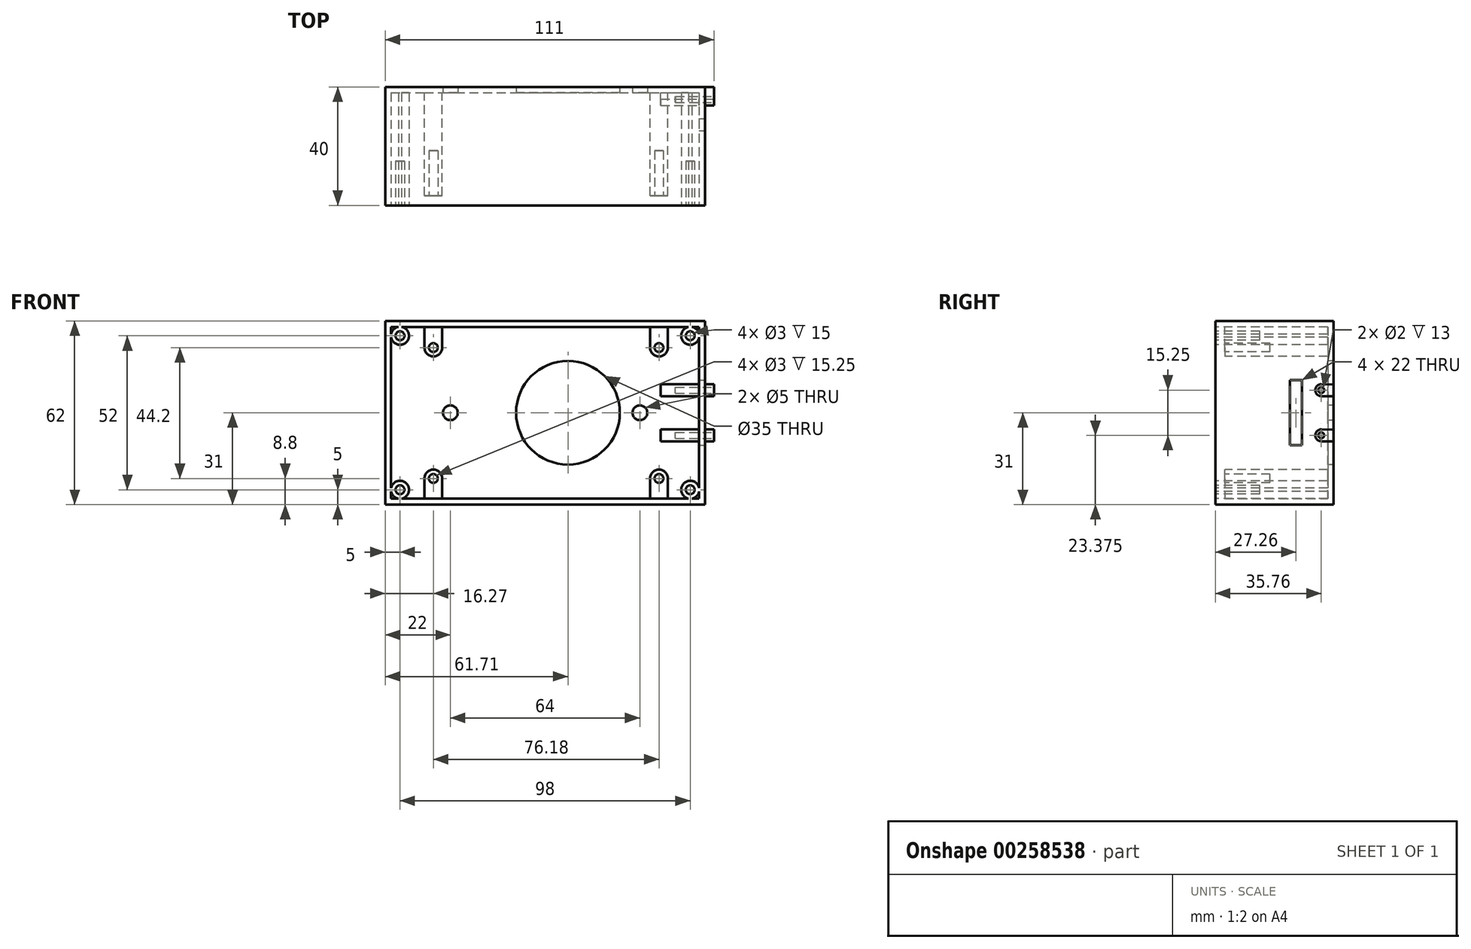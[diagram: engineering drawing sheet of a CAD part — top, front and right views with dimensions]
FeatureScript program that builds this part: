
annotation { "Feature Type Name" : "Feature", "Feature Type Description" : "" }
export const myFeature = defineFeature(function(context is Context, id is Id, definition is map)
    precondition{}
    {
        {
            var Q0;
            Q0=qCreatedBy(makeId("Front.planeOp"),FACE);
            var sketch = newSketch(context, id + "F0", { "sketchPlane" : qUnion([Q0])});
            skLineSegment(sketch, "E0.bottom", {"start": v(-54, 31) * mm, "end": v(54, 31) * mm});
            skLineSegment(sketch, "E0.top", {"start": v(-54, -31) * mm, "end": v(54, -31) * mm});
            skLineSegment(sketch, "E0.left", {"start": v(-54, 31) * mm, "end": v(-54, -31) * mm});
            skLineSegment(sketch, "E0.right", {"start": v(54, 31) * mm, "end": v(54, -31) * mm});
            skPoint(sketch, "E0.middle", {"position": v(0, 0) * mm});
            skSolve(sketch);
        }
        {
            var Q0;
            Q0 = qSketchRegion(id + "F0", true);
            extrude(context, id + "F1", {"entities" : qUnion([Q0]), "oppositeDirection" : true, "depth" : 40 * mm});
        }
        {
            var Q0;
            Q0=qCreatedBy(makeId("Front.planeOp"),FACE);
            var sketch = newSketch(context, id + "F2", { "sketchPlane" : qUnion([Q0])});
            skLineSegment(sketch, "E1.bottom", {"start": v(-52, 29) * mm, "end": v(52, 29) * mm});
            skLineSegment(sketch, "E1.top", {"start": v(-52, -29) * mm, "end": v(52, -29) * mm});
            skLineSegment(sketch, "E1.left", {"start": v(-52, 29) * mm, "end": v(-52, -29) * mm});
            skLineSegment(sketch, "E1.right", {"start": v(52, 29) * mm, "end": v(52, -29) * mm});
            skPoint(sketch, "E1.middle", {"position": v(0, 0) * mm});
            skSolve(sketch);
        }
        {
            var Q0;
            Q0 = qSketchRegion(id + "F2", true);
            extrude(context, id + "F3", {"entities" : qUnion([Q0]), "operationType" : NewBodyOperationType.REMOVE, "oppositeDirection" : true, "depth" : 38 * mm});
        }
        {
            var Q0;
            Q0=qCreatedBy(makeId("Front.planeOp"),FACE);
            var sketch = newSketch(context, id + "F4", { "sketchPlane" : qUnion([Q0])});
            skLineSegment(sketch, "E2", {"start": v(-34.65, 43.37) * mm, "end": v(34.65, 43.37) * mm, "construction": true});
            skCircle(sketch, "E3", {"center": v(-37.73, 43.37) * mm, "radius": 3 * mm, "construction": true});
            skCircle(sketch, "E4", {"center": v(38.45, 43.37) * mm, "radius": 3 * mm, "construction": true});
            skCircle(sketch, "E5", {"center": v(-37.73, 22) * mm, "radius": 3 * mm});
            skCircle(sketch, "E6", {"center": v(38.45, 22) * mm, "radius": 3 * mm});
            skCircle(sketch, "E7", {"center": v(-37.73, -22.2) * mm, "radius": 3 * mm});
            skCircle(sketch, "E8", {"center": v(38.45, -22.2) * mm, "radius": 3 * mm});
            skLineSegment(sketch, "E9", {"start": v(-40.73, 22) * mm, "end": v(-40.73, 29.02) * mm});
            skLineSegment(sketch, "E10", {"start": v(-34.73, 22) * mm, "end": v(-34.73, 29.02) * mm});
            skLineSegment(sketch, "E11", {"start": v(-40.73, 29.02) * mm, "end": v(-34.73, 29.02) * mm});
            skLineSegment(sketch, "E12", {"start": v(41.45, 22) * mm, "end": v(41.45, 29.1) * mm});
            skLineSegment(sketch, "E13", {"start": v(35.45, 22) * mm, "end": v(35.45, 29.1) * mm});
            skLineSegment(sketch, "E14", {"start": v(35.45, 29.1) * mm, "end": v(41.45, 29.1) * mm});
            skLineSegment(sketch, "E15", {"start": v(-40.73, -22.2) * mm, "end": v(-40.73, -29.27) * mm});
            skLineSegment(sketch, "E16", {"start": v(-34.73, -22.2) * mm, "end": v(-34.73, -29.29) * mm});
            skLineSegment(sketch, "E17", {"start": v(-34.73, -29.29) * mm, "end": v(-40.73, -29.27) * mm});
            skLineSegment(sketch, "E18", {"start": v(41.45, -22.2) * mm, "end": v(41.45, -29.3) * mm});
            skLineSegment(sketch, "E19", {"start": v(35.45, -22.2) * mm, "end": v(35.45, -29.3) * mm});
            skLineSegment(sketch, "E20", {"start": v(35.45, -29.3) * mm, "end": v(41.45, -29.3) * mm});
            skSolve(sketch);
        }
        {
            var Q0;
            Q0 = qSketchRegion(id + "F4", true);
            var Q1;
            Q1=makeQuery(id+"F3.boolean.opBoolean","COPY",FACE,{"derivedFrom":makeQuery(id+"F3.opExtrude","CAP_FACE",FACE,{"disambiguationData":[OSD([sQuery(id+"F2.wireOp",EDGE,"E1.bottom"),sQuery(id+"F2.wireOp",EDGE,"E1.top"),sQuery(id+"F2.wireOp",EDGE,"E1.left"),sQuery(id+"F2.wireOp",EDGE,"E1.right")])],"isStart":false})});
            extrude(context, id + "F5", {"entities" : qUnion([Q0]), "operationType" : NewBodyOperationType.ADD, "endBound" : BoundingType.UP_TO_SURFACE, "oppositeDirection" : true, "endBoundEntityFace" : qUnion([Q1]), "depth" : 25 * mm, "hasSecondDirection" : true, "secondDirectionOppositeDirection" : true, "secondDirectionDepth" : 3.25 * mm});
        }
        {
            var Q0;
            Q0=qCreatedBy(makeId("Front.planeOp"),FACE);
            var sketch = newSketch(context, id + "F6", { "sketchPlane" : qUnion([Q0])});
            skCircle(sketch, "E21", {"center": v(-49, 26) * mm, "radius": 3.05 * mm});
            skCircle(sketch, "E22", {"center": v(49, 26) * mm, "radius": 3.05 * mm});
            skCircle(sketch, "E23", {"center": v(49, -26) * mm, "radius": 3.05 * mm});
            skCircle(sketch, "E24", {"center": v(-49, -26) * mm, "radius": 3.05 * mm});
            skSolve(sketch);
        }
        {
            var Q0;
            Q0 = qSketchRegion(id + "F6", true);
            var Q1;
            Q1=makeQuery(id+"F3.boolean.opBoolean","COPY",FACE,{"derivedFrom":makeQuery(id+"F3.opExtrude","CAP_FACE",FACE,{"disambiguationData":[OSD([sQuery(id+"F2.wireOp",EDGE,"E1.bottom"),sQuery(id+"F2.wireOp",EDGE,"E1.top"),sQuery(id+"F2.wireOp",EDGE,"E1.left"),sQuery(id+"F2.wireOp",EDGE,"E1.right")])],"isStart":false})});
            extrude(context, id + "F7", {"entities" : qUnion([Q0]), "operationType" : NewBodyOperationType.ADD, "endBound" : BoundingType.UP_TO_SURFACE, "oppositeDirection" : true, "endBoundEntityFace" : qUnion([Q1]), "depth" : 25 * mm});
        }
        {
            var Q0;
            Q0=qCreatedBy(makeId("Front.planeOp"),FACE);
            var sketch = newSketch(context, id + "F8", { "sketchPlane" : qUnion([Q0])});
            skCircle(sketch, "E25", {"center": v(-49, 26) * mm, "radius": 1.5 * mm});
            skCircle(sketch, "E26", {"center": v(-49, -26) * mm, "radius": 1.5 * mm});
            skCircle(sketch, "E27", {"center": v(49, -26) * mm, "radius": 1.5 * mm});
            skCircle(sketch, "E28", {"center": v(49, 26) * mm, "radius": 1.5 * mm});
            skSolve(sketch);
        }
        {
            var Q0;
            Q0 = qSketchRegion(id + "F8", true);
            extrude(context, id + "F9", {"entities" : qUnion([Q0]), "operationType" : NewBodyOperationType.REMOVE, "oppositeDirection" : true, "depth" : 15 * mm});
        }
        {
            var Q0;
            Q0=qCreatedBy(makeId("Front.planeOp"),FACE);
            var sketch = newSketch(context, id + "F10", { "sketchPlane" : qUnion([Q0])});
            skLineSegment(sketch, "E29", {"start": v(-34.65, 43.4) * mm, "end": v(34.65, 43.4) * mm, "construction": true});
            skCircle(sketch, "E30", {"center": v(-37.73, 43.4) * mm, "radius": 3 * mm, "construction": true});
            skCircle(sketch, "E31", {"center": v(38.45, 43.4) * mm, "radius": 3 * mm, "construction": true});
            skCircle(sketch, "E32", {"center": v(-37.73, 22) * mm, "radius": 1.5 * mm});
            skCircle(sketch, "E33", {"center": v(-37.73, -22.2) * mm, "radius": 1.5 * mm});
            skCircle(sketch, "E34", {"center": v(38.45, 22) * mm, "radius": 1.5 * mm});
            skCircle(sketch, "E35", {"center": v(38.45, -22.2) * mm, "radius": 1.5 * mm});
            skSolve(sketch);
        }
        {
            var Q0;
            Q0 = qSketchRegion(id + "F10", true);
            extrude(context, id + "F11", {"entities" : qUnion([Q0]), "operationType" : NewBodyOperationType.REMOVE, "oppositeDirection" : true, "depth" : 18.5 * mm});
        }
        {
            var Q0;
            Q0=qCreatedBy(makeId("Front.planeOp"),FACE);
            var sketch = newSketch(context, id + "F12", { "sketchPlane" : qUnion([Q0])});
            skCircle(sketch, "E36", {"center": v(7.71, 0) * mm, "radius": 17.5 * mm});
            skCircle(sketch, "E37", {"center": v(-32, 0) * mm, "radius": 2.5 * mm});
            skCircle(sketch, "E38", {"center": v(32, 0) * mm, "radius": 2.5 * mm});
            skSolve(sketch);
        }
        {
            var Q0;
            Q0 = qSketchRegion(id + "F12", true);
            extrude(context, id + "F13", {"entities" : qUnion([Q0]), "operationType" : NewBodyOperationType.REMOVE, "endBound" : BoundingType.THROUGH_ALL, "oppositeDirection" : true, "depth" : 25 * mm});
        }
        {
            var Q0;
            Q0=makeQuery(id+"F1.opExtrude","SWEPT_FACE",FACE,{"disambiguationData":[OSD([sQuery(id+"F0.wireOp",EDGE,"E0.right")])]});
            cPlane(context, id + "F14", {"entities" : qUnion([Q0]), "cplaneType" : CPlaneType.OFFSET, "offset" : 0 * mm, "width" : 150 * mm, "height" : 150 * mm});
        }
        {
            var Q0;
            Q0=qCreatedBy(id+"F14.planeOp",FACE);
            var sketch = newSketch(context, id + "F15", { "sketchPlane" : qUnion([Q0])});
            skArc(sketch, "E39", {"start": v(35.79, 9.62) * mm, "mid": v(33.76, 7.6) * mm, "end": v(35.85, 5.63) * mm});
            skArc(sketch, "E40", {"start": v(35.82, -5.63) * mm, "mid": v(33.76, -7.6) * mm, "end": v(35.77, -9.62) * mm});
            skLineSegment(sketch, "E41.0", {"start": v(40, 31) * mm, "end": v(40, -31) * mm, "construction": true});
            skLineSegment(sketch, "E42", {"start": v(35.79, 9.62) * mm, "end": v(40, 9.57) * mm});
            skLineSegment(sketch, "E43", {"start": v(35.85, 5.63) * mm, "end": v(40, 5.63) * mm});
            skLineSegment(sketch, "E44", {"start": v(35.82, -5.63) * mm, "end": v(40, -5.74) * mm});
            skLineSegment(sketch, "E45", {"start": v(35.75, -9.62) * mm, "end": v(40, -9.62) * mm});
            skLineSegment(sketch, "E46", {"start": v(40, 9.57) * mm, "end": v(40, 5.63) * mm});
            skLineSegment(sketch, "E47", {"start": v(40, -5.74) * mm, "end": v(40, -9.62) * mm});
            skSolve(sketch);
        }
        {
            var Q0;
            Q0 = qSketchRegion(id + "F15", true);
            extrude(context, id + "F16", {"entities" : qUnion([Q0]), "operationType" : NewBodyOperationType.ADD, "oppositeDirection" : true, "depth" : 15 * mm, "hasSecondDirection" : true, "secondDirectionOppositeDirection" : false, "secondDirectionDepth" : 3 * mm});
        }
        {
            var Q0;
            Q0=qCreatedBy(id+"F14.planeOp",FACE);
            var sketch = newSketch(context, id + "F17", { "sketchPlane" : qUnion([Q0])});
            skLineSegment(sketch, "E48.bottom", {"start": v(29.26, -11) * mm, "end": v(25.26, -11) * mm});
            skLineSegment(sketch, "E48.top", {"start": v(29.26, 11) * mm, "end": v(25.26, 11) * mm});
            skLineSegment(sketch, "E48.left", {"start": v(29.26, -11) * mm, "end": v(29.26, 11) * mm});
            skLineSegment(sketch, "E48.right", {"start": v(25.26, -11) * mm, "end": v(25.26, 11) * mm});
            skPoint(sketch, "E48.middle", {"position": v(27.26, 0) * mm});
            skArc(sketch, "E49.0.1", {"start": v(35.85, 5.63) * mm, "mid": v(33.76, 7.6) * mm, "end": v(35.79, 9.62) * mm, "construction": true});
            skArc(sketch, "E49.0.3", {"start": v(35.79, 9.62) * mm, "mid": v(33.76, 7.6) * mm, "end": v(35.85, 5.63) * mm, "construction": true});
            skArc(sketch, "E50.0.1", {"start": v(35.75, -9.62) * mm, "mid": v(33.76, -7.6) * mm, "end": v(35.82, -5.63) * mm, "construction": true});
            skArc(sketch, "E50.0.3", {"start": v(35.82, -5.63) * mm, "mid": v(33.76, -7.6) * mm, "end": v(35.75, -9.62) * mm, "construction": true});
            skSolve(sketch);
        }
        {
            var Q0;
            Q0=makeQuery(id+"F17.imprint","IMPRINT",FACE,{"disambiguationData":[TD([[makeQuery(id+"F17.imprint","IMPRINT",EDGE,{"derivedFrom":sQuery(id+"F17.wireOp",EDGE,"E48.bottom")}),-1.0]])]});
            var Q1;
            {var subQ0=sQuery(id+"F6.wireOp",EDGE,"E22");var subQ1=sQuery(id+"F2.wireOp",EDGE,"E1.right");var subQ2=sQuery(id+"F6.wireOp",EDGE,"E23");Q1=makeQuery(id+"F7.boolean.opBoolean","SPLIT",FACE,{"disambiguationData":[TD([makeQuery(id+"F1.opExtrude","CAP_FACE",FACE,{"disambiguationData":[OSD([sQuery(id+"F0.wireOp",EDGE,"E0.bottom"),sQuery(id+"F0.wireOp",EDGE,"E0.top"),sQuery(id+"F0.wireOp",EDGE,"E0.left"),sQuery(id+"F0.wireOp",EDGE,"E0.right")])],"isStart":true}),makeQuery(id+"F3.boolean.opBoolean","COPY",FACE,{"derivedFrom":makeQuery(id+"F3.opExtrude","CAP_FACE",FACE,{"disambiguationData":[OSD([sQuery(id+"F2.wireOp",EDGE,"E1.bottom"),sQuery(id+"F2.wireOp",EDGE,"E1.top"),sQuery(id+"F2.wireOp",EDGE,"E1.left"),subQ1])],"isStart":false})}),makeQuery(id+"F7.opExtrude","CAP_FACE",FACE,{"disambiguationData":[OSD([sQuery(id+"F6.wireOp",EDGE,"E21")])],"isStart":true}),makeQuery(id+"F7.opExtrude","SWEPT_FACE",FACE,{"disambiguationData":[OSD([subQ0])]}),makeQuery(id+"F7.opExtrude","CAP_FACE",FACE,{"disambiguationData":[OSD([subQ0])],"isStart":true}),makeQuery(id+"F7.opExtrude","SWEPT_FACE",FACE,{"disambiguationData":[OSD([subQ2])]}),makeQuery(id+"F7.opExtrude","CAP_FACE",FACE,{"disambiguationData":[OSD([subQ2])],"isStart":true}),makeQuery(id+"F7.opExtrude","CAP_FACE",FACE,{"disambiguationData":[OSD([sQuery(id+"F6.wireOp",EDGE,"E24")])],"isStart":true})])],"derivedFrom":makeQuery(id+"F3.boolean.opBoolean","COPY",FACE,{"derivedFrom":makeQuery(id+"F3.opExtrude","SWEPT_FACE",FACE,{"disambiguationData":[OSD([subQ1])]})})});}
            extrude(context, id + "F18", {"entities" : qUnion([Q0]), "operationType" : NewBodyOperationType.REMOVE, "endBound" : BoundingType.UP_TO_SURFACE, "oppositeDirection" : true, "endBoundEntityFace" : qUnion([Q1]), "depth" : 25 * mm});
        }
        {
            var Q0;
            Q0=qCreatedBy(id+"F14.planeOp",FACE);
            var sketch = newSketch(context, id + "F19", { "sketchPlane" : qUnion([Q0])});
            skArc(sketch, "E51.0.1", {"start": v(35.85, 5.63) * mm, "mid": v(33.76, 7.6) * mm, "end": v(35.79, 9.62) * mm, "construction": true});
            skArc(sketch, "E51.0.3", {"start": v(35.79, 9.62) * mm, "mid": v(33.76, 7.6) * mm, "end": v(35.85, 5.63) * mm, "construction": true});
            skArc(sketch, "E52.0.1", {"start": v(35.75, -9.62) * mm, "mid": v(33.76, -7.6) * mm, "end": v(35.82, -5.63) * mm, "construction": true});
            skArc(sketch, "E52.0.3", {"start": v(35.82, -5.63) * mm, "mid": v(33.76, -7.6) * mm, "end": v(35.75, -9.62) * mm, "construction": true});
            skCircle(sketch, "E53", {"center": v(35.76, 7.62) * mm, "radius": 1 * mm});
            skCircle(sketch, "E54", {"center": v(35.76, -7.63) * mm, "radius": 1 * mm});
            skSolve(sketch);
        }
        {
            var Q0;
            Q0 = qSketchRegion(id + "F19", true);
            extrude(context, id + "F20", {"entities" : qUnion([Q0]), "operationType" : NewBodyOperationType.REMOVE, "oppositeDirection" : true, "depth" : 10 * mm, "hasSecondDirection" : true, "secondDirectionOppositeDirection" : false, "secondDirectionDepth" : 5 * mm});
        }
    });
